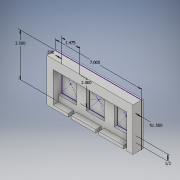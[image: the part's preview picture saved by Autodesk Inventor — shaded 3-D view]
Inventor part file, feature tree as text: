
AUTODESK INVENTOR PART (.ipt)
format: ipt  version: 2018 (Build 220112000, 112)  size: 161,792 bytes
history: native  units: in
note: dims shown in document units (in); Inventor stores cm internally (conversion verified against a paired STEP export)
features: extrude x4, sketch x2, pattern_linear x1
ambient origin geometry x8: Origin, YZ Plane, XZ Plane, XY Plane, X Axis, Y Axis, Z Axis, Center Point
bodies: Solid1 (feature_tree)
feature tree (7):
  sketch  "Sketch1"  dims[d0=7.0in d1=3.5in]
  extrude  "Extrusion1"  Depth=3.5in
  extrude  "Extrusion2"  Depth=2.0in
  extrude  "Extrusion3"  Depth=0.5in
  extrude  "Extrusion4"  Depth=0.5in
  pattern_linear  "Rectangular Pattern1"  Spacing1=0.5in  [1 undecoded]
  sketch  "Sketch2"  dims[d2=1.475in d3=2.0in d4=0.5in d5=0.5in d6=0.5in d7=0.7in d8=0.0in d9=0.125in d10=0.0in d11=0.25in d12=0.0in d13=0.25in d14=0.25in d15=0.0in d16=1.1811in d18=2.25in]
note: 1 required parameter value undecoded (feature->parameter linkage not recoverable at this tier; creation-order binding heuristic only, values carry confidence <= 0.55)
